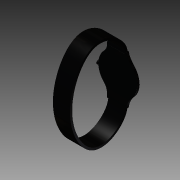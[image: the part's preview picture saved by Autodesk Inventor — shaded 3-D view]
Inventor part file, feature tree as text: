
AUTODESK INVENTOR PART (.ipt)
format: ipt  version: 2013 SP1 (Build 170176100, 176)  size: 1,657,856 bytes
history: native  units: mm
features: sketch x26, extrude x11, plane x10, fillet x5, emboss x4, sweep x3, mirror x2, pattern_circular x2, loft x2, delete_face x1, chamfer x1
ambient origin geometry x8: Origin, YZ Plane, XZ Plane, XY Plane, X Axis, Y Axis, Z Axis, Center Point
bodies: Solid1 (feature_tree)
feature tree (67):
  sweep  "Sweep1"
  extrude  "Extrusion1"  TaperAngle=0.0deg  [1 undecoded]
  mirror  "Mirror1"
  emboss  "Emboss3"
  plane  "Work Plane5"
  plane  "Work Plane6"
  sketch  "Sketch12"  dims[d79=-3.175mm d94=0.0mm]
  extrude  "Extrusion2"  Depth=0.45mm TaperAngle=0.0deg
  plane  "Work Plane10"
  plane  "Work Plane9"
  sweep  "Sweep3"
  extrude  "Extrusion4"  TaperAngle=0.0deg  [1 undecoded]
  extrude  "Extrusion5"  Depth=0.275mm TaperAngle=0.0deg
  mirror  "Mirror4"
  plane  "Work Plane13"
  extrude  "Extrusion6"  [1 undecoded]
  extrude  "Extrusion7"  Depth=0.75mm
  fillet  "Fillet2"  Radius=0.25mm
  fillet  "Fillet3"  Radius=0.05mm
  extrude  "Extrusion8"  Depth=0.005mm TaperAngle=0.0deg
  pattern_circular  "Circular Pattern6"  Count=12 Angle=360.0deg
  delete_face  "Delete Face7"
  pattern_circular  "Circular Pattern7"  Count=12 Angle=360.0deg
  chamfer  "Chamfer4"  Distance=0.38mm Angle=45.0deg
  fillet  "Fillet4"  Radius=4.0mm
  emboss  "Emboss4"
  emboss  "Emboss5"
  extrude  "Extrusion9"  Depth=0.005mm TaperAngle=0.0deg
  fillet  "Fillet5"  Radius=6.5mm
  fillet  "Fillet6"  Radius=0.05mm
  sketch  "Sketch33"  dims[d208=0.25mm]
  sweep  "Sweep4"
  emboss  "Emboss6"
  plane  "Work Plane16"
  extrude  "Extrusion10"  Depth=0.175mm
  extrude  "Extrusion11"  Depth=0.0075mm TaperAngle=0.0deg
  extrude  "Extrusion12"  Depth=0.05mm
  plane  "Work Plane17"
  loft  "Loft4"
  plane  "Work Plane18"
  loft  "Loft5"
  sketch  "Sketch1"  dims[d2=0.0mm d3=8.0mm]
  sketch  "Sketch2"  dims[d4=0.5mm d5=0.0mm d6=0.0mm]
  sketch  "Sketch3"  dims[d23=0.5mm d24=0.45mm d25=0.0mm]
  sketch  "Sketch6"  dims[d46=-0.08mm d70=10.0mm d71=0.0mm]
  sketch  "Sketch15"  dims[d107=0.075mm d108=0.275mm d109=0.0mm]
  sketch  "Sketch20"  dims[d112=3.75mm d113=0.0mm d114=-4.0mm]
  sketch  "Sketch21"  dims[d116=0.025mm d117=0.0mm d119=0.75mm d120=0.25mm d121=0.0mm d122=0.05mm]
  sketch  "Sketch23"  dims[d123=0.0125mm d125=0.005mm d126=0.0mm d130=120.0mm d131=360.0deg d133=120.0mm d134=360.0deg d136=0.38mm d137=2.0mm d138=45.0deg d139=4.0mm]
  sketch  "Sketch24"  dims[d151=0.005mm d152=0.0mm d155=0.005mm d156=0.0mm d157=6.5mm d158=0.05mm d159=0.0mm]
  sketch  "Sketch25"  dims[d160=0.075mm d161=0.025mm]
  sketch  "Sketch27"  dims[d167=0.0mm d171=0.175mm]
  sketch  "Sketch28"  dims[d172=0.175mm d173=0.0075mm d174=0.0mm]
  sketch  "Sketch30"  dims[d175=0.125mm d176=0.05mm d177=0.05mm]
  sketch  "Sketch31"  dims[d184=0.02mm d185=0.0mm d192=0.02mm d193=0.0mm]
  sketch  "Sketch32"  dims[d194=0.02mm d206=0.02mm d207=0.0mm]
  sketch  "Sketch34"  dims[d209=0.0mm d210=90.0deg d211=20.0mm d212=90.0deg]
  sketch  "Sketch35"  dims[d213=-0.025mm]
  plane  "Work Plane14"
  plane  "Work Plane15"
  sketch  "Sketch36"  dims[d214=6.5mm]
  sketch  "Sketch37"  dims[d215=0.0mm d216=90.0deg d217=10.0mm d218=90.0deg]
  sketch  "Sketch38"
  sketch  "Sketch39"
  sketch  "Sketch40"
  sketch  "Sketch42"
  sketch  "Sketch43"
note: 3 required parameter values undecoded (feature->parameter linkage not recoverable at this tier; creation-order binding heuristic only, values carry confidence <= 0.55)
